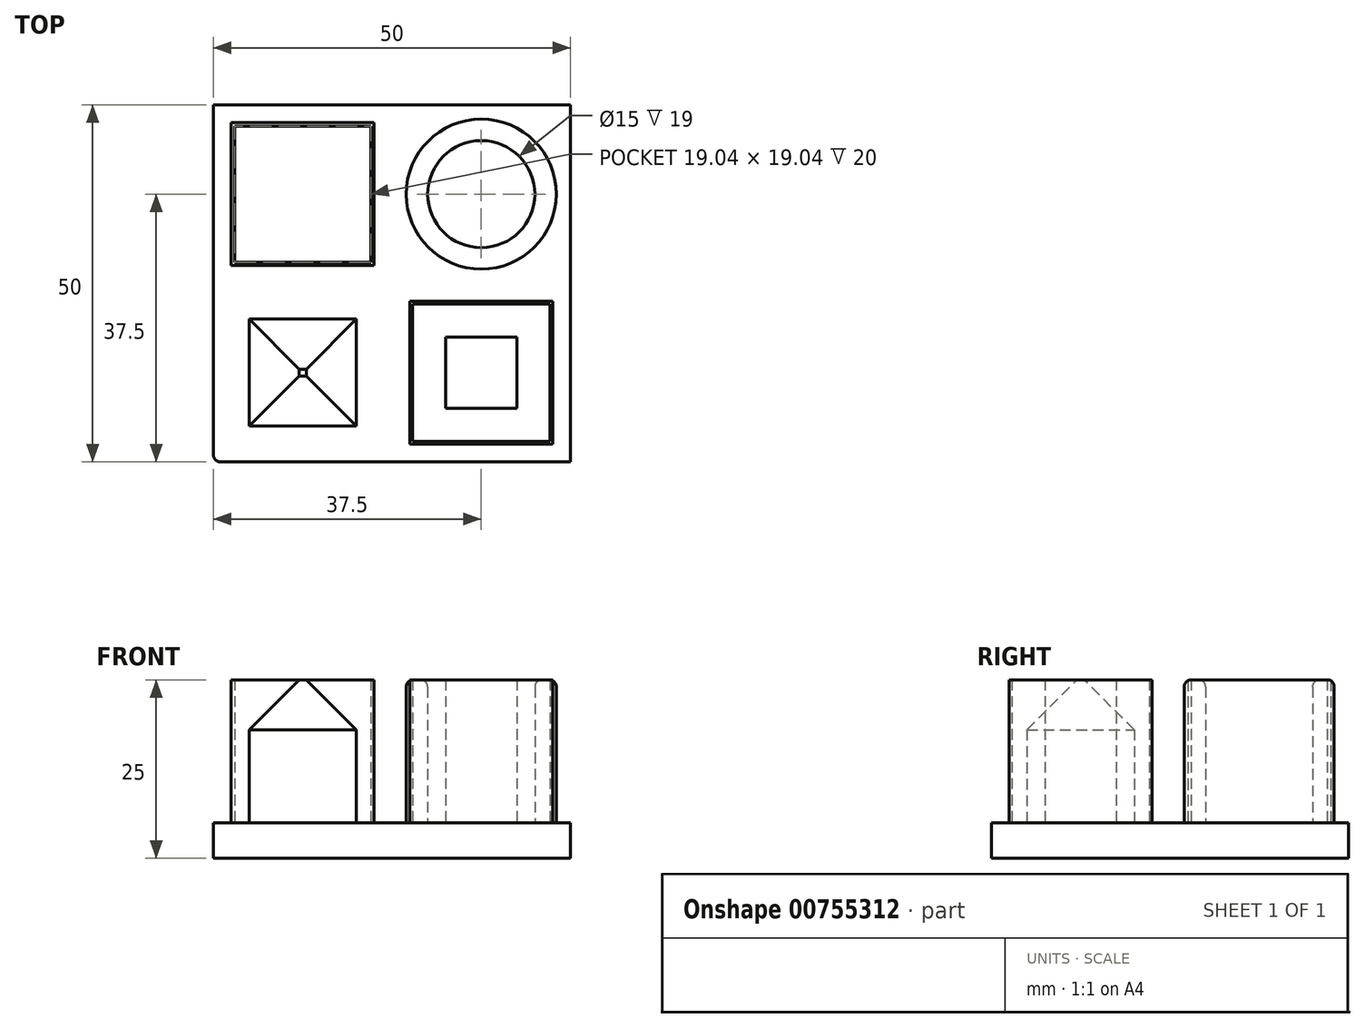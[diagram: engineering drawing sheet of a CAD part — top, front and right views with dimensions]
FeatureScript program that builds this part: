
annotation { "Feature Type Name" : "Feature", "Feature Type Description" : "" }
export const myFeature = defineFeature(function(context is Context, id is Id, definition is map)
    precondition{}
    {
        {
            var Q0;
            Q0=qCreatedBy(makeId("Top.planeOp"),FACE);
            var sketch = newSketch(context, id + "F0", { "sketchPlane" : qUnion([Q0])});
            skLineSegment(sketch, "E0.bottom", {"start": v(-25, 25) * mm, "end": v(25, 25) * mm});
            skLineSegment(sketch, "E0.top", {"start": v(-25, -25) * mm, "end": v(25, -25) * mm});
            skLineSegment(sketch, "E0.left", {"start": v(-25, 25) * mm, "end": v(-25, -25) * mm});
            skLineSegment(sketch, "E0.right", {"start": v(25, 25) * mm, "end": v(25, -25) * mm});
            skLineSegment(sketch, "E1.bottom", {"start": v(-22.5, 22.5) * mm, "end": v(-2.5, 22.5) * mm});
            skLineSegment(sketch, "E1.top", {"start": v(-22.5, 2.5) * mm, "end": v(-2.5, 2.5) * mm});
            skLineSegment(sketch, "E1.left", {"start": v(-22.5, 22.5) * mm, "end": v(-22.5, 2.5) * mm});
            skLineSegment(sketch, "E1.right", {"start": v(-2.5, 22.5) * mm, "end": v(-2.5, 2.5) * mm});
            skLineSegment(sketch, "E2.0", {"start": v(-22.02, 22.02) * mm, "end": v(-2.98, 22.02) * mm});
            skLineSegment(sketch, "E2.1", {"start": v(-22.02, 22.02) * mm, "end": v(-22.02, 2.98) * mm});
            skLineSegment(sketch, "E2.2", {"start": v(-22.02, 2.98) * mm, "end": v(-2.98, 2.98) * mm});
            skLineSegment(sketch, "E2.3", {"start": v(-2.98, 22.02) * mm, "end": v(-2.98, 2.98) * mm});
            skLineSegment(sketch, "E3.bottom", {"start": v(2.5, -2.5) * mm, "end": v(22.5, -2.5) * mm});
            skLineSegment(sketch, "E3.top", {"start": v(2.5, -22.5) * mm, "end": v(22.5, -22.5) * mm});
            skLineSegment(sketch, "E3.left", {"start": v(2.5, -2.5) * mm, "end": v(2.5, -22.5) * mm});
            skLineSegment(sketch, "E3.right", {"start": v(22.5, -2.5) * mm, "end": v(22.5, -22.5) * mm});
            skLineSegment(sketch, "E4.0", {"start": v(2.9, -2.9) * mm, "end": v(22.1, -2.9) * mm});
            skLineSegment(sketch, "E4.1", {"start": v(2.9, -2.9) * mm, "end": v(2.9, -22.1) * mm});
            skLineSegment(sketch, "E4.2", {"start": v(2.9, -22.1) * mm, "end": v(22.1, -22.1) * mm});
            skLineSegment(sketch, "E4.3", {"start": v(22.1, -2.9) * mm, "end": v(22.1, -22.1) * mm});
            skLineSegment(sketch, "E5.bottom", {"start": v(7.5, -7.5) * mm, "end": v(17.5, -7.5) * mm});
            skLineSegment(sketch, "E5.top", {"start": v(7.5, -17.5) * mm, "end": v(17.5, -17.5) * mm});
            skLineSegment(sketch, "E5.left", {"start": v(7.5, -7.5) * mm, "end": v(7.5, -17.5) * mm});
            skLineSegment(sketch, "E5.right", {"start": v(17.5, -7.5) * mm, "end": v(17.5, -17.5) * mm});
            skLineSegment(sketch, "E6.bottom", {"start": v(17.5, -10.7) * mm, "end": v(22.1, -10.7) * mm, "construction": true});
            skLineSegment(sketch, "E6.top", {"start": v(17.5, -10.78) * mm, "end": v(22.1, -10.78) * mm, "construction": true});
            skLineSegment(sketch, "E6.left", {"start": v(17.5, -10.7) * mm, "end": v(17.5, -10.78) * mm, "construction": true});
            skLineSegment(sketch, "E6.right", {"start": v(22.1, -10.7) * mm, "end": v(22.1, -10.78) * mm, "construction": true});
            skLineSegment(sketch, "E7.bottom", {"start": v(7.5, -10.7) * mm, "end": v(2.9, -10.7) * mm, "construction": true});
            skLineSegment(sketch, "E7.top", {"start": v(7.5, -10.7) * mm, "end": v(2.9, -10.7) * mm, "construction": true});
            skLineSegment(sketch, "E7.left", {"start": v(7.5, -10.7) * mm, "end": v(7.5, -10.7) * mm});
            skLineSegment(sketch, "E7.right", {"start": v(2.9, -10.7) * mm, "end": v(2.9, -10.7) * mm});
            skLineSegment(sketch, "E8", {"start": v(12.5, -7.5) * mm, "end": v(12.5, -2.9) * mm, "construction": true});
            skLineSegment(sketch, "E9", {"start": v(12.5, -17.5) * mm, "end": v(12.5, -22.1) * mm, "construction": true});
            skLineSegment(sketch, "E10.bottom", {"start": v(-20, -5) * mm, "end": v(-5, -5) * mm});
            skLineSegment(sketch, "E10.top", {"start": v(-20, -20) * mm, "end": v(-5, -20) * mm});
            skLineSegment(sketch, "E10.left", {"start": v(-20, -5) * mm, "end": v(-20, -20) * mm});
            skLineSegment(sketch, "E10.right", {"start": v(-5, -5) * mm, "end": v(-5, -20) * mm});
            skLineSegment(sketch, "E11", {"start": v(-20, -12.5) * mm, "end": v(-25, -12.5) * mm, "construction": true});
            skLineSegment(sketch, "E12", {"start": v(-12.5, -20) * mm, "end": v(-12.5, -25) * mm, "construction": true});
            skLineSegment(sketch, "E13", {"start": v(-5, -12.5) * mm, "end": v(0, -12.5) * mm, "construction": true});
            skLineSegment(sketch, "E14", {"start": v(-12.5, -5) * mm, "end": v(-12.5, 0) * mm, "construction": true});
            skLineSegment(sketch, "E15", {"start": v(0, 12.5) * mm, "end": v(25, 12.5) * mm, "construction": true});
            skPoint(sketch, "E15.startSnap0", {"position": v(-2.5, 12.5) * mm});
            skLineSegment(sketch, "E16", {"start": v(12.5, 12.5) * mm, "end": v(12.5, 25) * mm, "construction": true});
            skCircle(sketch, "E17", {"center": v(12.5, 12.5) * mm, "radius": 7.5 * mm});
            skCircle(sketch, "E18.0", {"center": v(12.5, 12.5) * mm, "radius": 10.5 * mm});
            skSolve(sketch);
        }
        {
            var Q0;
            Q0 = qSketchRegion(id + "F0", true);
            var Q1;
            Q1=makeQuery(id+"F0.imprint","IMPRINT",FACE,{"disambiguationData":[TD([[makeQuery(id+"F0.imprint","IMPRINT",EDGE,{"derivedFrom":sQuery(id+"F0.wireOp",EDGE,"E2.0")}),-1.0]])]});
            var Q2;
            Q2=makeQuery(id+"F0.imprint","IMPRINT",FACE,{"disambiguationData":[TD([[makeQuery(id+"F0.imprint","IMPRINT",EDGE,{"derivedFrom":sQuery(id+"F0.wireOp",EDGE,"E1.bottom")}),-1.0]])]});
            var Q3;
            Q3=makeQuery(id+"F0.imprint","IMPRINT",FACE,{"disambiguationData":[TD([[makeQuery(id+"F0.imprint","IMPRINT",EDGE,{"derivedFrom":sQuery(id+"F0.wireOp",EDGE,"E17")}),-1.0]])]});
            var Q4;
            Q4=makeQuery(id+"F0.imprint","IMPRINT",FACE,{"disambiguationData":[TD([[makeQuery(id+"F0.imprint","IMPRINT",EDGE,{"derivedFrom":sQuery(id+"F0.wireOp",EDGE,"E17")}),1.0]])]});
            var Q5;
            Q5=makeQuery(id+"F0.imprint","IMPRINT",FACE,{"disambiguationData":[TD([[makeQuery(id+"F0.imprint","IMPRINT",EDGE,{"derivedFrom":sQuery(id+"F0.wireOp",EDGE,"E10.bottom")}),-1.0]])]});
            var Q6;
            Q6=makeQuery(id+"F0.imprint","IMPRINT",FACE,{"disambiguationData":[TD([[makeQuery(id+"F0.imprint","IMPRINT",EDGE,{"derivedFrom":sQuery(id+"F0.wireOp",EDGE,"E3.bottom")}),-1.0]])]});
            var Q7;
            Q7=makeQuery(id+"F0.imprint","IMPRINT",FACE,{"disambiguationData":[TD([[makeQuery(id+"F0.imprint","IMPRINT",EDGE,{"derivedFrom":sQuery(id+"F0.wireOp",EDGE,"E4.0")}),-1.0]])]});
            var Q8;
            Q8=makeQuery(id+"F0.imprint","IMPRINT",FACE,{"disambiguationData":[TD([[makeQuery(id+"F0.imprint","IMPRINT",EDGE,{"derivedFrom":sQuery(id+"F0.wireOp",EDGE,"E5.bottom")}),-1.0]])]});
            extrude(context, id + "F1", {"entities" : qUnion([Q0, Q1, Q2, Q3, Q4, Q5, Q6, Q7, Q8]), "depth" : 5 * mm, "offsetDistance" : 25 * mm});
        }
        {
            var Q0;
            Q0=makeQuery(id+"F0.imprint","IMPRINT",FACE,{"disambiguationData":[TD([[makeQuery(id+"F0.imprint","IMPRINT",EDGE,{"derivedFrom":sQuery(id+"F0.wireOp",EDGE,"E1.bottom")}),-1.0]])]});
            extrude(context, id + "F2", {"entities" : qUnion([Q0]), "operationType" : NewBodyOperationType.ADD, "depth" : 25 * mm, "offsetDistance" : 25 * mm});
        }
        {
            var Q0;
            Q0=makeQuery(id+"F0.imprint","IMPRINT",FACE,{"disambiguationData":[TD([[makeQuery(id+"F0.imprint","IMPRINT",EDGE,{"derivedFrom":sQuery(id+"F0.wireOp",EDGE,"E3.bottom")}),-1.0]])]});
            var Q1;
            Q1=makeQuery(id+"F0.imprint","IMPRINT",FACE,{"disambiguationData":[TD([[makeQuery(id+"F0.imprint","IMPRINT",EDGE,{"derivedFrom":sQuery(id+"F0.wireOp",EDGE,"E5.bottom")}),-1.0]])]});
            extrude(context, id + "F3", {"entities" : qUnion([Q0, Q1]), "operationType" : NewBodyOperationType.ADD, "depth" : 25 * mm, "offsetDistance" : 25 * mm});
        }
        {
            var Q0;
            Q0=makeQuery(id+"F0.imprint","IMPRINT",FACE,{"disambiguationData":[TD([[makeQuery(id+"F0.imprint","IMPRINT",EDGE,{"derivedFrom":sQuery(id+"F0.wireOp",EDGE,"E10.bottom")}),-1.0]])]});
            extrude(context, id + "F4", {"entities" : qUnion([Q0]), "operationType" : NewBodyOperationType.ADD, "depth" : 25 * mm, "offsetDistance" : 25 * mm});
        }
        {
            var Q0;
            Q0=makeQuery(id+"F0.imprint","IMPRINT",FACE,{"disambiguationData":[TD([[makeQuery(id+"F0.imprint","IMPRINT",EDGE,{"derivedFrom":sQuery(id+"F0.wireOp",EDGE,"E17")}),-1.0]])]});
            extrude(context, id + "F5", {"entities" : qUnion([Q0]), "operationType" : NewBodyOperationType.ADD, "depth" : 25 * mm, "offsetDistance" : 25 * mm});
        }
        {
            var Q0;
            Q0=makeQuery(id+"F1.opExtrude","SWEPT_EDGE",EDGE,{"disambiguationData":[OSD([sQuery(id+"F0.wireOp",EDGE,"E0.top"),sQuery(id+"F0.wireOp",EDGE,"E0.left")])]});
            var Q1;
            Q1=makeQuery(id+"F5.opExtrude","CAP_FACE",FACE,{"disambiguationData":[OSD([sQuery(id+"F0.wireOp",EDGE,"E17"),sQuery(id+"F0.wireOp",EDGE,"E18.0")])],"isStart":false});
            fillet(context, id + "F6", {"entities" : qUnion([Q0, Q1]), "radius" : 1 * mm, "tangentPropagation" : true, "allowEdgeOverflow" : false});
        }
        {
            var Q0;
            Q0=makeQuery(id+"F4.opExtrude","CAP_FACE",FACE,{"disambiguationData":[OSD([sQuery(id+"F0.wireOp",EDGE,"E10.bottom"),sQuery(id+"F0.wireOp",EDGE,"E10.top"),sQuery(id+"F0.wireOp",EDGE,"E10.left"),sQuery(id+"F0.wireOp",EDGE,"E10.right")])],"isStart":false});
            chamfer(context, id + "F7", {"entities" : qUnion([Q0]), "width" : 7 * mm, "tangentPropagation" : true});
        }
    });
